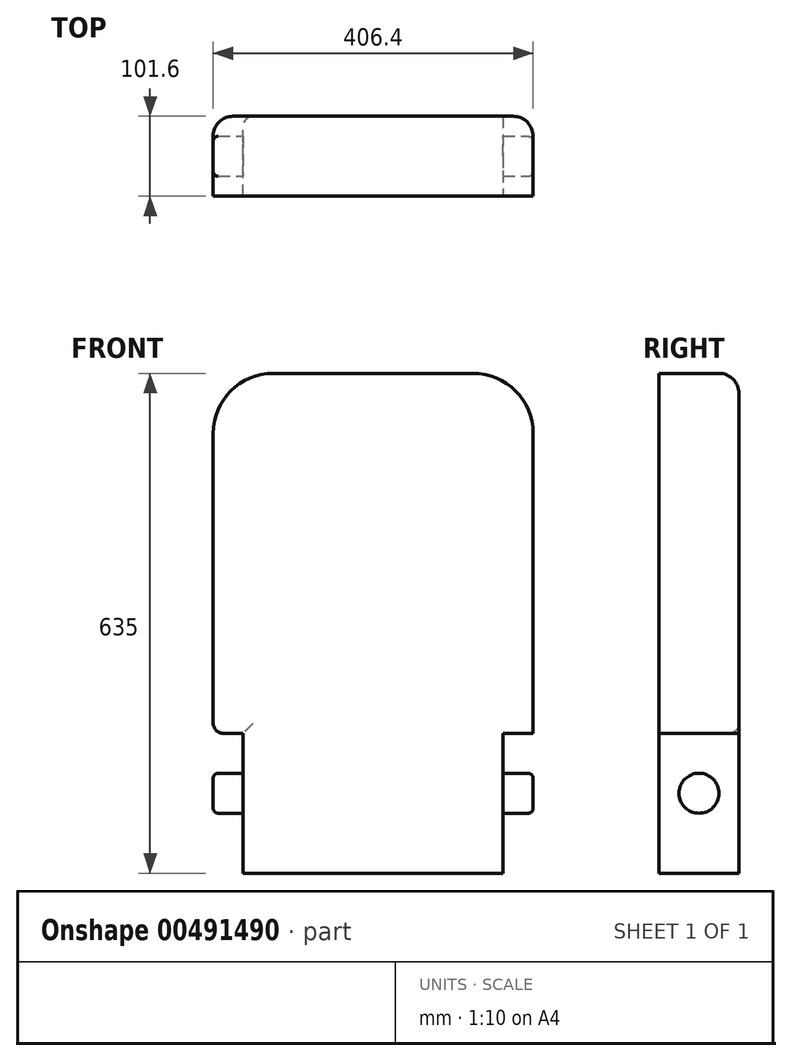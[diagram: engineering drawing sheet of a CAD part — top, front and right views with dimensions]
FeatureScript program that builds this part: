
annotation { "Feature Type Name" : "Feature", "Feature Type Description" : "" }
export const myFeature = defineFeature(function(context is Context, id is Id, definition is map)
    precondition{}
    {
        {
            var Q0;
            Q0=qCreatedBy(makeId("Front.planeOp"),FACE);
            var sketch = newSketch(context, id + "F0", { "sketchPlane" : qUnion([Q0])});
            skLineSegment(sketch, "E0.bottom", {"start": v(-207.44, 414.12) * mm, "end": v(198.96, 414.12) * mm});
            skLineSegment(sketch, "E0.top", {"start": v(-207.44, -220.88) * mm, "end": v(198.96, -220.88) * mm});
            skLineSegment(sketch, "E0.left", {"start": v(-207.44, 414.12) * mm, "end": v(-207.44, -220.88) * mm});
            skLineSegment(sketch, "E0.right", {"start": v(198.96, 414.12) * mm, "end": v(198.96, -220.88) * mm});
            skSolve(sketch);
        }
        {
            var Q0;
            Q0=makeQuery(id+"F0.imprint","IMPRINT",FACE,{"disambiguationData":[TD([[makeQuery(id+"F0.imprint","IMPRINT",EDGE,{"derivedFrom":sQuery(id+"F0.wireOp",EDGE,"E0.bottom")}),-1.0]])]});
            extrude(context, id + "F1", {"entities" : qUnion([Q0]), "depth" : 101.6 * mm});
        }
        {
            var Q0;
            Q0=makeQuery(id+"F1.opExtrude","CAP_FACE",FACE,{"disambiguationData":[OSD([sQuery(id+"F0.wireOp",EDGE,"E0.bottom"),sQuery(id+"F0.wireOp",EDGE,"E0.top"),sQuery(id+"F0.wireOp",EDGE,"E0.left"),sQuery(id+"F0.wireOp",EDGE,"E0.right")])],"isStart":false});
            var sketch = newSketch(context, id + "F2", { "sketchPlane" : qUnion([Q0])});
            skLineSegment(sketch, "E1.bottom", {"start": v(-169.34, -602.24) * mm, "end": v(-298.97, -602.24) * mm});
            skLineSegment(sketch, "E1.top", {"start": v(-169.34, -43.08) * mm, "end": v(-298.97, -43.08) * mm});
            skLineSegment(sketch, "E1.left", {"start": v(-169.34, -602.24) * mm, "end": v(-169.34, -43.08) * mm});
            skLineSegment(sketch, "E1.right", {"start": v(-298.97, -602.24) * mm, "end": v(-298.97, -43.08) * mm});
            skPoint(sketch, "E2.startSnap0", {"position": v(-4.24, -220.88) * mm});
            skLineSegment(sketch, "E3.bottom", {"start": v(160.86, -43.08) * mm, "end": v(391.6, -43.08) * mm});
            skLineSegment(sketch, "E3.top", {"start": v(160.86, -530.01) * mm, "end": v(391.6, -530.01) * mm});
            skLineSegment(sketch, "E3.left", {"start": v(160.86, -43.08) * mm, "end": v(160.86, -530.01) * mm});
            skLineSegment(sketch, "E3.right", {"start": v(391.6, -43.08) * mm, "end": v(391.6, -530.01) * mm});
            skSolve(sketch);
        }
        {
            var Q0;
            Q0=qSketchRegion(id+"F2",true);
            extrude(context, id + "F3", {"entities" : qUnion([Q0]), "operationType" : NewBodyOperationType.REMOVE, "oppositeDirection" : true, "depth" : 127 * mm});
        }
        {
            var Q0;
            Q0=makeQuery(id+"F1.opExtrude","SWEPT_EDGE",EDGE,{"disambiguationData":[OSD([sQuery(id+"F0.wireOp",EDGE,"E0.bottom"),sQuery(id+"F0.wireOp",EDGE,"E0.right")])]});
            var Q1;
            Q1=makeQuery(id+"F1.opExtrude","SWEPT_EDGE",EDGE,{"disambiguationData":[OSD([sQuery(id+"F0.wireOp",EDGE,"E0.bottom"),sQuery(id+"F0.wireOp",EDGE,"E0.left")])]});
            fillet(context, id + "F4", {"entities" : qUnion([Q0, Q1]), "radius" : 76.2 * mm, "tangentPropagation" : true, "allowEdgeOverflow" : false});
        }
        {
            var Q0;
            Q0=makeQuery(id+"F1.opExtrude","CAP_EDGE",EDGE,{"disambiguationData":[OSD([sQuery(id+"F0.wireOp",EDGE,"E0.right")])],"isStart":true});
            var Q1;
            {var subQ0=sQuery(id+"F0.wireOp",EDGE,"E0.right");var subQ1=sQuery(id+"F0.wireOp",EDGE,"E0.bottom");Q1=makeQuery(id+"F4.opFillet","BLEND_EDGE",EDGE,{"blendedFrom":[makeQuery(id+"F1.opExtrude","SWEPT_EDGE",EDGE,{"disambiguationData":[OSD([subQ1,subQ0])]}),makeQuery(id+"F1.opExtrude","CAP_FACE",FACE,{"disambiguationData":[OSD([subQ1,sQuery(id+"F0.wireOp",EDGE,"E0.top"),sQuery(id+"F0.wireOp",EDGE,"E0.left"),subQ0])],"isStart":true})],"blendedInto":[makeQuery(id+"F1.opExtrude","CAP_FACE",FACE,{"disambiguationData":[OSD([subQ1,sQuery(id+"F0.wireOp",EDGE,"E0.top"),sQuery(id+"F0.wireOp",EDGE,"E0.left"),subQ0])],"isStart":true})]});}
            var Q2;
            Q2=makeQuery(id+"F1.opExtrude","CAP_EDGE",EDGE,{"disambiguationData":[OSD([sQuery(id+"F0.wireOp",EDGE,"E0.bottom")])],"isStart":true});
            var Q3;
            {var subQ0=sQuery(id+"F0.wireOp",EDGE,"E0.left");var subQ1=sQuery(id+"F0.wireOp",EDGE,"E0.bottom");Q3=makeQuery(id+"F4.opFillet","BLEND_EDGE",EDGE,{"blendedFrom":[makeQuery(id+"F1.opExtrude","SWEPT_EDGE",EDGE,{"disambiguationData":[OSD([subQ1,subQ0])]}),makeQuery(id+"F1.opExtrude","CAP_FACE",FACE,{"disambiguationData":[OSD([subQ1,sQuery(id+"F0.wireOp",EDGE,"E0.top"),subQ0,sQuery(id+"F0.wireOp",EDGE,"E0.right")])],"isStart":true})],"blendedInto":[makeQuery(id+"F1.opExtrude","CAP_FACE",FACE,{"disambiguationData":[OSD([subQ1,sQuery(id+"F0.wireOp",EDGE,"E0.top"),subQ0,sQuery(id+"F0.wireOp",EDGE,"E0.right")])],"isStart":true})]});}
            var Q4;
            Q4=makeQuery(id+"F1.opExtrude","CAP_EDGE",EDGE,{"disambiguationData":[OSD([sQuery(id+"F0.wireOp",EDGE,"E0.left")])],"isStart":true});
            fillet(context, id + "F5", {"entities" : qUnion([Q0, Q1, Q2, Q3, Q4]), "radius" : 25.4 * mm, "tangentPropagation" : true, "allowEdgeOverflow" : false});
        }
        {
            var Q0;
            Q0=makeQuery(id+"F1.opExtrude","SWEPT_FACE",FACE,{"disambiguationData":[OSD([sQuery(id+"F0.wireOp",EDGE,"E0.right")])]});
            var sketch = newSketch(context, id + "F6", { "sketchPlane" : qUnion([Q0])});
            skCircle(sketch, "E4", {"center": v(-50.8, -119.28) * mm, "radius": 25.4 * mm});
            skSolve(sketch);
        }
        {
            var Q0;
            Q0=makeQuery(id+"F6.imprint","IMPRINT",FACE,{"disambiguationData":[TD([[makeQuery(id+"F6.imprint","IMPRINT",EDGE,{"derivedFrom":sQuery(id+"F6.wireOp",EDGE,"E4")}),1.0]])]});
            extrude(context, id + "F7", {"entities" : qUnion([Q0]), "operationType" : NewBodyOperationType.ADD, "oppositeDirection" : true, "depth" : 406.4 * mm, "hasSecondDirection" : true, "secondDirectionOppositeDirection" : true, "secondDirectionDepth" : 0 * mm});
        }
        {
            var Q0;
            Q0=makeQuery(id+"F7.opExtrude","CAP_EDGE",EDGE,{"disambiguationData":[OSD([sQuery(id+"F6.wireOp",EDGE,"E4")])],"isStart":false});
            var Q1;
            Q1=makeQuery(id+"F7.opExtrude","CAP_EDGE",EDGE,{"disambiguationData":[OSD([sQuery(id+"F6.wireOp",EDGE,"E4")])],"isStart":true});
            fillet(context, id + "F8", {"entities" : qUnion([Q0, Q1]), "radius" : 6.35 * mm, "tangentPropagation" : true, "allowEdgeOverflow" : false});
        }
        {
            var Q0;
            Q0=makeQuery(id+"F3.boolean.opBoolean","INTERSECT",EDGE,{"derivedFrom":[makeQuery(id+"F1.opExtrude","CAP_FACE",FACE,{"disambiguationData":[OSD([sQuery(id+"F0.wireOp",EDGE,"E0.bottom"),sQuery(id+"F0.wireOp",EDGE,"E0.top"),sQuery(id+"F0.wireOp",EDGE,"E0.left"),sQuery(id+"F0.wireOp",EDGE,"E0.right")])],"isStart":true}),makeQuery(id+"F3.opExtrude","SWEPT_FACE",FACE,{"disambiguationData":[OSD([sQuery(id+"F2.wireOp",EDGE,"f0eaf16c-8975-4743-9150-ccc82628e9d80.MirrorCS")])]})]});
            var Q1;
            Q1=makeQuery(id+"F3.boolean.opBoolean","INTERSECT",EDGE,{"derivedFrom":[makeQuery(id+"F1.opExtrude","SWEPT_FACE",FACE,{"disambiguationData":[OSD([sQuery(id+"F0.wireOp",EDGE,"E0.right")])]}),makeQuery(id+"F3.opExtrude","SWEPT_FACE",FACE,{"disambiguationData":[OSD([sQuery(id+"F2.wireOp",EDGE,"9571ceae-20ac-4f51-ad11-72628280eaa70.MirrorCS")])]})]});
            var Q2;
            Q2=makeQuery(id+"F5.opFillet","BLEND_EDGE",EDGE,{"blendedFrom":[makeQuery(id+"F1.opExtrude","CAP_EDGE",EDGE,{"disambiguationData":[OSD([sQuery(id+"F0.wireOp",EDGE,"E0.right")])],"isStart":true}),makeQuery(id+"F3.boolean.opBoolean","COPY",FACE,{"derivedFrom":makeQuery(id+"F3.opExtrude","SWEPT_FACE",FACE,{"disambiguationData":[OSD([sQuery(id+"F2.wireOp",EDGE,"9571ceae-20ac-4f51-ad11-72628280eaa70.MirrorCS")])]})})],"blendedInto":[makeQuery(id+"F3.boolean.opBoolean","COPY",FACE,{"derivedFrom":makeQuery(id+"F3.opExtrude","SWEPT_FACE",FACE,{"disambiguationData":[OSD([sQuery(id+"F2.wireOp",EDGE,"9571ceae-20ac-4f51-ad11-72628280eaa70.MirrorCS")])]})})]});
            var Q3;
            Q3=makeQuery(id+"F3.boolean.opBoolean","INTERSECT",EDGE,{"derivedFrom":[makeQuery(id+"F1.opExtrude","CAP_FACE",FACE,{"disambiguationData":[OSD([sQuery(id+"F0.wireOp",EDGE,"E0.bottom"),sQuery(id+"F0.wireOp",EDGE,"E0.top"),sQuery(id+"F0.wireOp",EDGE,"E0.left"),sQuery(id+"F0.wireOp",EDGE,"E0.right")])],"isStart":true}),makeQuery(id+"F3.opExtrude","SWEPT_FACE",FACE,{"disambiguationData":[OSD([sQuery(id+"F2.wireOp",EDGE,"9571ceae-20ac-4f51-ad11-72628280eaa70.MirrorCS")])]})]});
            var Q4;
            Q4=makeQuery(id+"F3.boolean.opBoolean","INTERSECT",EDGE,{"derivedFrom":[makeQuery(id+"F1.opExtrude","CAP_FACE",FACE,{"disambiguationData":[OSD([sQuery(id+"F0.wireOp",EDGE,"E0.bottom"),sQuery(id+"F0.wireOp",EDGE,"E0.top"),sQuery(id+"F0.wireOp",EDGE,"E0.left"),sQuery(id+"F0.wireOp",EDGE,"E0.right")])],"isStart":true}),makeQuery(id+"F3.opExtrude","SWEPT_FACE",FACE,{"disambiguationData":[OSD([sQuery(id+"F2.wireOp",EDGE,"E1.left")])]})]});
            var Q5;
            Q5=makeQuery(id+"F3.boolean.opBoolean","INTERSECT",EDGE,{"derivedFrom":[makeQuery(id+"F1.opExtrude","CAP_FACE",FACE,{"disambiguationData":[OSD([sQuery(id+"F0.wireOp",EDGE,"E0.bottom"),sQuery(id+"F0.wireOp",EDGE,"E0.top"),sQuery(id+"F0.wireOp",EDGE,"E0.left"),sQuery(id+"F0.wireOp",EDGE,"E0.right")])],"isStart":true}),makeQuery(id+"F3.opExtrude","SWEPT_FACE",FACE,{"disambiguationData":[OSD([sQuery(id+"F2.wireOp",EDGE,"E1.top")])]})]});
            var Q6;
            Q6=makeQuery(id+"F5.opFillet","BLEND_EDGE",EDGE,{"blendedFrom":[makeQuery(id+"F1.opExtrude","CAP_EDGE",EDGE,{"disambiguationData":[OSD([sQuery(id+"F0.wireOp",EDGE,"E0.left")])],"isStart":true}),makeQuery(id+"F3.boolean.opBoolean","COPY",FACE,{"derivedFrom":makeQuery(id+"F3.opExtrude","SWEPT_FACE",FACE,{"disambiguationData":[OSD([sQuery(id+"F2.wireOp",EDGE,"E1.top")])]})})],"blendedInto":[makeQuery(id+"F3.boolean.opBoolean","COPY",FACE,{"derivedFrom":makeQuery(id+"F3.opExtrude","SWEPT_FACE",FACE,{"disambiguationData":[OSD([sQuery(id+"F2.wireOp",EDGE,"E1.top")])]})})]});
            var Q7;
            Q7=makeQuery(id+"F3.boolean.opBoolean","INTERSECT",EDGE,{"derivedFrom":[makeQuery(id+"F1.opExtrude","SWEPT_FACE",FACE,{"disambiguationData":[OSD([sQuery(id+"F0.wireOp",EDGE,"E0.left")])]}),makeQuery(id+"F3.opExtrude","SWEPT_FACE",FACE,{"disambiguationData":[OSD([sQuery(id+"F2.wireOp",EDGE,"E1.top")])]})]});
            fillet(context, id + "F9", {"entities" : qUnion([Q0, Q1, Q2, Q3, Q4, Q5, Q6, Q7]), "radius" : 12.7 * mm, "tangentPropagation" : true, "allowEdgeOverflow" : false});
        }
        {
            var Q0;
            Q0=qSketchRegion(id+"F2",true);
            extrude(context, id + "F10", {"entities" : qUnion([Q0]), "operationType" : NewBodyOperationType.REMOVE, "oppositeDirection" : true, "depth" : 25.4 * mm});
        }
    });
